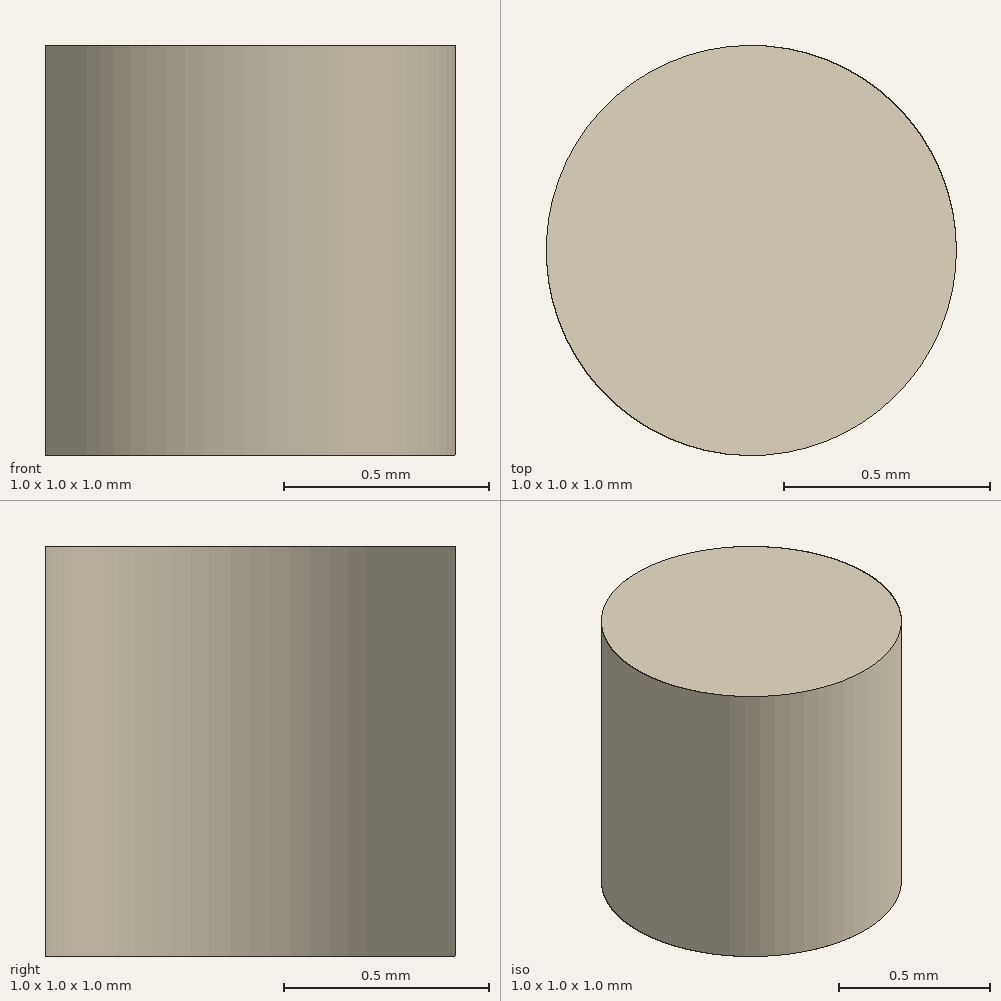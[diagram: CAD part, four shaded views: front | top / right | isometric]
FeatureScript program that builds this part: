
annotation { "Feature Type Name" : "Feature", "Feature Type Description" : "" }
export const myFeature = defineFeature(function(context is Context, id is Id, definition is map)
    precondition{}
    {
        {
            var Q0;
            Q0=qCreatedBy(makeId("Top.planeOp"),FACE);
            var sketch = newSketch(context, id + "F0", { "sketchPlane" : qUnion([Q0])});
            skCircle(sketch, "E0", {"center": v(0, 0) * mm, "radius": 0.5 * mm});
            skSolve(sketch);
        }
        {
            var Q0;
            Q0 = qSketchRegion(id + "F0", true);
            extrude(context, id + "F1", {"entities" : qUnion([Q0]), "depth" : .5 * mm, "hasSecondDirection" : true, "secondDirectionOppositeDirection" : true, "secondDirectionDepth" : .5 * mm});
        }
    });
